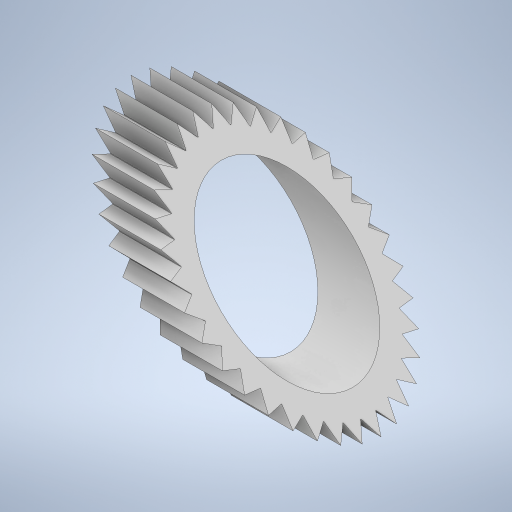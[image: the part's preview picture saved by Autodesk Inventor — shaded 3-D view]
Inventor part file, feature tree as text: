
AUTODESK INVENTOR PART (.ipt)
format: ipt  version: 2023 (Build 270158030, 158C)  size: 433,664 bytes
history: native  units: in
note: dims shown in document units (in); Inventor stores cm internally (conversion verified against a paired STEP export)
features: extrude x3, sketch x3
ambient origin geometry x8: Origin, YZ Plane, XZ Plane, XY Plane, X Axis, Y Axis, Z Axis, Center Point
bodies: Solid1 (feature_tree)
feature tree (6):
  extrude  "Extrusion1"  Depth=13.3858in TaperAngle=360.0deg
  extrude  "Extrusion3"  TaperAngle=45.0deg  [1 undecoded]
  extrude  "Extrusion4"  Depth=0.25in TaperAngle=0.0deg
  sketch  "Sketch1"  dims[d0=60.0deg d1=13.3858in d3=360.0deg]
  sketch  "Sketch2"  dims[d5=2.0in d6=0.0in d7=45.0deg]
  sketch  "Sketch3"  dims[d8=0.25in d11=2.0in d12=0.0in d13=2.0in d14=0.0in d15=0.75in]
note: 1 required parameter value undecoded (feature->parameter linkage not recoverable at this tier; creation-order binding heuristic only, values carry confidence <= 0.55)
